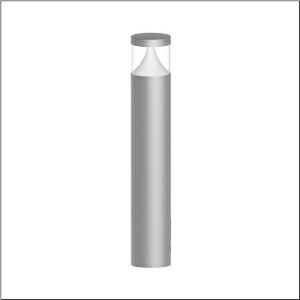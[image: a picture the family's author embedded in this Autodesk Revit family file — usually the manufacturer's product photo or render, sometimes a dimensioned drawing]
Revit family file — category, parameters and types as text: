
# Revit family: cl_31_poller_90_5cl444603
name_source: partatom
category: Lighting Fixtures
units: mm (PartAtom-declared; Revit-internal decimal feet)

## family parameters
Cut with Voids When Loaded = No
Host = Face
Light Source = No
Part Type = Normal
Room Calculation Point = No
Round Connector Dimension = Use Diameter
Shared = No

## types (1)
- --- (1 x LED, 1500 lm, 14 W, 3000K)
    Apparent Load = 14 VA
    CIE Flux Codes = 19 66 88 92 100
    Color Rendering = 80
    Color Temperature = 3000K
    Default Elevation = 1800 mm
    Description = CL 31 Bollard 90, bollard luminaire, primary light control with lens, of PC, primary optical cover: cover panel, of PC, transparent, secondary light control with reflector, of PC, primary light characteristic: asymmetric, LED, rated luminous flux: 1.500lm, luminous efficacy: 107lm/W, light colour: 830, colour temperature: 3000K, control gear: ECG DALI, with terminal, 5-pole, max. 2.5mm², mains connection: 220..240V, AC, 50/60Hz, rated input power: 14W, luminaire housing, of aluminium, powder-coated, Siteco® metallic grey, diameter: 170mm, height: 900mm, protection rating (complete): IP65, insulation class (complete): insulation class I (protective earthing), certification: CE, ENEC, impact resistance: IK10, permissible operating ambient temperature for outdoor applications: -20..+50°C, packaging unit: 1 piece
    Height = 200 mm
    Lamp = 1 x LED
    Lamp Light Flux = 1500 lm
    Lamp Power = 14 W
    Lamp count = 1
    Length = 170 mm
    Luminous efficacy = 107 lm/W
    Manufacturer = Siteco
    ModVariant = No
    Model = 5CL444603
    Mounting Place = Floor
    Mounting Type = Freestanding
    Number of Poles = 1
    OnlyDefault = Yes
    Power Factor = 1
    Product Name = CL 31 Poller 90
    Product group = bollard luminaire
    ProductGroupID = 1304
    Protection Class = Protection class I
    Protection Degree = IP 65
    RLX_Detail_Level = 1
    RLX_Emergency_Light_Flux = 0 lm
    RLX_Emergency_Type = 0
    RLX_Emergency_Type_DB = No
    RlxData = <blob elided: 65553 chars, md5=bf057d1d>
    Socket = socket
    Standby Power = 0 W
    System Light Flux = 1500 lm
    System Power = 14 W
    Type Comments = factory setting: luminous flux: 100 % | dim-lin: 254 | 350 mA
    Type Image = l_1006899.jpg
    URL = http://relux.com
    VarID = @adj_130331
    Voltage = 0 V
    Weight = 0.00 kg
    Width = 0 mm  [stored 0 ft]

note: [stored X ft] marks values corroborated as IEEE doubles in the binary element streams (Revit-internal decimal feet)

## geometry (parser evidence)
native form markers: Blend x4, Sweep x10
no freeform markers — native parametric forms only
